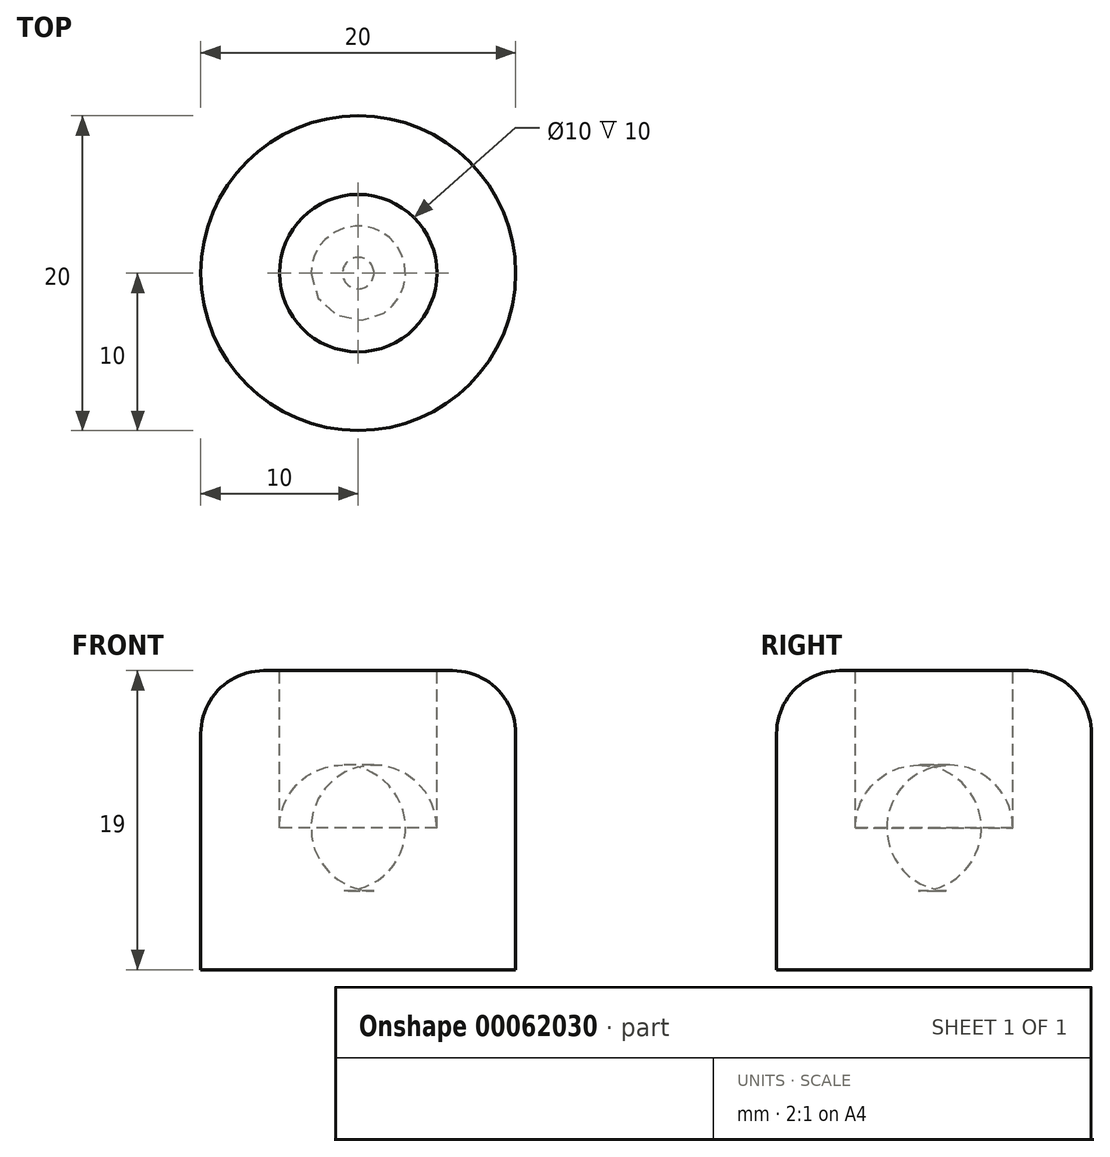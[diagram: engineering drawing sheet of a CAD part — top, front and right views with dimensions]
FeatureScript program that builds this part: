
annotation { "Feature Type Name" : "Feature", "Feature Type Description" : "" }
export const myFeature = defineFeature(function(context is Context, id is Id, definition is map)
    precondition{}
    {
        {
            var Q0;
            Q0=qCreatedBy(makeId("Front.planeOp"),FACE);
            var sketch = newSketch(context, id + "F0", { "sketchPlane" : qUnion([Q0])});
            skLineSegment(sketch, "E0", {"start": v(-5, 5.63) * mm, "end": v(-5, -4.37) * mm});
            skLineSegment(sketch, "E1", {"start": v(-1, -8.37) * mm, "end": v(0, -8.37) * mm});
            skLineSegment(sketch, "E2", {"start": v(0, -8.37) * mm, "end": v(0, -13.37) * mm});
            skLineSegment(sketch, "E3", {"start": v(0, -13.37) * mm, "end": v(-10, -13.37) * mm});
            skLineSegment(sketch, "E4", {"start": v(-10, -13.37) * mm, "end": v(-10, 1.63) * mm});
            skLineSegment(sketch, "E5", {"start": v(-6, 5.63) * mm, "end": v(-5, 5.63) * mm});
            skPoint(sketch, "E6.visualSharp", {"position": v(-10, 5.63) * mm});
            skArc(sketch, "E6.filletArc", {"start": v(-6, 5.63) * mm, "mid": v(-8.83, 4.46) * mm, "end": v(-10, 1.63) * mm});
            skPoint(sketch, "E7.visualSharp", {"position": v(-5, -8.37) * mm});
            skArc(sketch, "E7.filletArc", {"start": v(-5, -4.37) * mm, "mid": v(-3.83, -7.2) * mm, "end": v(-1, -8.37) * mm});
            skSolve(sketch);
        }
        {
            var Q0;
            Q0 = qSketchRegion(id + "F0", true);
            var Q1;
            Q1=sQuery(id+"F0.wireOp",EDGE,"E2");
            revolve(context, id + "F1", {"entities" : qUnion([Q0]), "axis" : qUnion([Q1]), "revolveType" : RevolveType.FULL});
        }
    });
